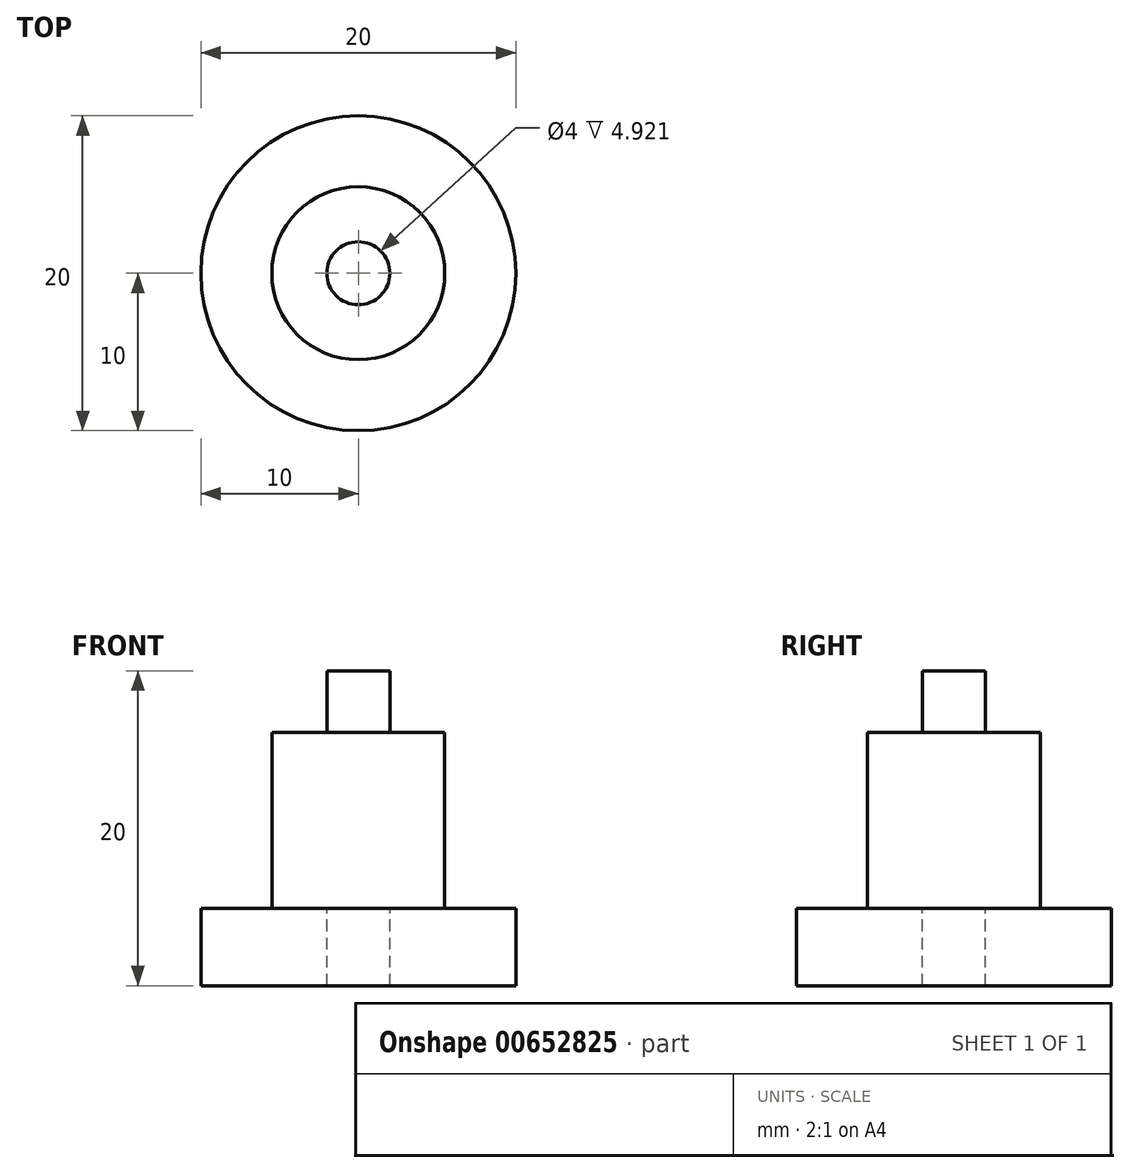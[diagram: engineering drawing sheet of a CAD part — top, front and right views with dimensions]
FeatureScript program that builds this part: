
annotation { "Feature Type Name" : "Feature", "Feature Type Description" : "" }
export const myFeature = defineFeature(function(context is Context, id is Id, definition is map)
    precondition{}
    {
        {
            var Q0;
            Q0=qCreatedBy(makeId("Front.planeOp"),FACE);
            var sketch = newSketch(context, id + "F0", { "sketchPlane" : qUnion([Q0])});
            skLineSegment(sketch, "E0.bottom", {"start": v(0, 2.34) * mm, "end": v(10, 2.34) * mm});
            skLineSegment(sketch, "E0.top", {"start": v(0, -2.26) * mm, "end": v(10, -2.26) * mm});
            skLineSegment(sketch, "E0.left", {"start": v(0, 2.34) * mm, "end": v(0, -2.26) * mm});
            skLineSegment(sketch, "E0.right", {"start": v(10, 2.34) * mm, "end": v(10, -2.26) * mm});
            skLineSegment(sketch, "E1", {"start": v(2, 2.34) * mm, "end": v(2, -2.26) * mm});
            skSolve(sketch);
        }
        {
            var Q0;
            {var subQ0=sQuery(id+"F0.wireOp",EDGE,"E0.right");Q0=makeQuery(id+"F0.imprint","IMPRINT",FACE,{"disambiguationData":[TD([[makeQuery(id+"F0.imprint","IMPRINT",EDGE,{"derivedFrom":subQ0}),-1.0]])]});}
            var Q1;
            Q1=sQuery(id+"F0.wireOp",EDGE,"E0.left");
            revolve(context, id + "F1", {"entities" : qUnion([Q0]), "axis" : qUnion([Q1]), "revolveType" : RevolveType.FULL});
        }
        {
            var Q0;
            Q0=makeQuery(id+"F1.opRevolve","SWEPT_FACE",FACE,{"disambiguationData":[OSD([sQuery(id+"F0.wireOp",EDGE,"E0.bottom")])]});
            var sketch = newSketch(context, id + "F2", { "sketchPlane" : qUnion([Q0])});
            skCircle(sketch, "E2.0", {"center": v(0, 0) * mm, "radius": 5.5 * mm});
            skSolve(sketch);
        }
        {
            var Q0;
            Q0=makeQuery(id+"F2.imprint","IMPRINT",FACE,{"disambiguationData":[TD([[makeQuery(id+"F2.imprint","IMPRINT",EDGE,{"derivedFrom":sQuery(id+"F2.wireOp",EDGE,"E2.0")}),1.0]])]});
            extrude(context, id + "F3", {"entities" : qUnion([Q0]), "operationType" : NewBodyOperationType.ADD, "depth" : .3 * mm, "offsetDistance" : 25 * mm});
        }
        {
            var Q0;
            Q0=qCreatedBy(makeId("Front.planeOp"),FACE);
            var sketch = newSketch(context, id + "F4", { "sketchPlane" : qUnion([Q0])});
            skLineSegment(sketch, "E3.bottom", {"start": v(0, 2.65) * mm, "end": v(5.5, 2.65) * mm});
            skLineSegment(sketch, "E3.top", {"start": v(0, 13.85) * mm, "end": v(5.5, 13.85) * mm});
            skLineSegment(sketch, "E3.left", {"start": v(0, 2.65) * mm, "end": v(0, 13.85) * mm});
            skLineSegment(sketch, "E3.right", {"start": v(5.5, 2.65) * mm, "end": v(5.5, 13.85) * mm});
            skSolve(sketch);
        }
        {
            var Q0;
            Q0 = qSketchRegion(id + "F4", true);
            var Q1;
            Q1=sQuery(id+"F4.wireOp",EDGE,"E3.left");
            revolve(context, id + "F5", {"entities" : qUnion([Q0]), "axis" : qUnion([Q1]), "revolveType" : RevolveType.FULL});
        }
        {
            var Q0;
            Q0=makeQuery(id+"F5.opRevolve","SWEPT_FACE",FACE,{"disambiguationData":[OSD([sQuery(id+"F4.wireOp",EDGE,"E3.top")])]});
            var sketch = newSketch(context, id + "F6", { "sketchPlane" : qUnion([Q0])});
            skCircle(sketch, "E4.0", {"center": v(0, 0) * mm, "radius": 2 * mm});
            skSolve(sketch);
        }
        {
            var Q0;
            Q0=makeQuery(id+"F6.imprint","IMPRINT",FACE,{"disambiguationData":[TD([[makeQuery(id+"F6.imprint","IMPRINT",EDGE,{"derivedFrom":sQuery(id+"F6.wireOp",EDGE,"E4.0")}),1.0]])]});
            extrude(context, id + "F7", {"entities" : qUnion([Q0]), "operationType" : NewBodyOperationType.ADD, "depth" : 3.9 * mm, "offsetDistance" : 25 * mm});
        }
        {
            var Q0;
            Q0=qCreatedBy(makeId("Front.planeOp"),FACE);
            var sketch = newSketch(context, id + "F8", { "sketchPlane" : qUnion([Q0])});
            skLineSegment(sketch, "E5", {"start": v(0, 17.77) * mm, "end": v(2, 17.77) * mm});
            skLineSegment(sketch, "E6", {"start": v(2, 17.77) * mm, "end": v(2, 13.87) * mm});
            skLineSegment(sketch, "E7", {"start": v(2, 13.87) * mm, "end": v(5.5, 13.87) * mm});
            skLineSegment(sketch, "E8", {"start": v(5.5, 13.87) * mm, "end": v(5.5, 2.67) * mm});
            skLineSegment(sketch, "E9", {"start": v(5.5, 2.67) * mm, "end": v(10, 2.67) * mm});
            skLineSegment(sketch, "E10", {"start": v(10, 2.67) * mm, "end": v(10, -2.23) * mm});
            skLineSegment(sketch, "E11", {"start": v(10, -2.23) * mm, "end": v(2, -2.23) * mm});
            skLineSegment(sketch, "E12", {"start": v(2, -2.23) * mm, "end": v(2, 2.7) * mm});
            skLineSegment(sketch, "E13", {"start": v(2, 2.7) * mm, "end": v(0, 2.7) * mm});
            skLineSegment(sketch, "E14", {"start": v(0, 2.7) * mm, "end": v(0, 17.77) * mm});
            skLineSegment(sketch, "E15", {"start": v(0, 23.76) * mm, "end": v(0, -14.34) * mm});
            skSolve(sketch);
        }
        {
            var Q0;
            {var subQ0=sQuery(id+"F8.wireOp",EDGE,"E5");Q0=makeQuery(id+"F8.imprint","IMPRINT",FACE,{"disambiguationData":[TD([[makeQuery(id+"F8.imprint","IMPRINT",EDGE,{"derivedFrom":subQ0}),-1.0]])]});}
            var Q1;
            Q1=sQuery(id+"F8.wireOp",EDGE,"E15");
            revolve(context, id + "F9", {"entities" : qUnion([Q0]), "axis" : qUnion([Q1]), "revolveType" : RevolveType.FULL});
        }
        {
            var Q0;
            Q0=makeQuery(id+"F1.opRevolve","SWEPT_BODY",BODY,{"disambiguationData":[OSD([sQuery(id+"F0.wireOp",EDGE,"E0.bottom"),sQuery(id+"F0.wireOp",EDGE,"E0.top"),sQuery(id+"F0.wireOp",EDGE,"E0.right"),sQuery(id+"F0.wireOp",EDGE,"E1")])]});
            var Q1;
            Q1=makeQuery(id+"F5.opRevolve","SWEPT_BODY",BODY,{"disambiguationData":[OSD([sQuery(id+"F4.wireOp",EDGE,"E3.bottom"),sQuery(id+"F4.wireOp",EDGE,"E3.top"),sQuery(id+"F4.wireOp",EDGE,"E3.left"),sQuery(id+"F4.wireOp",EDGE,"E3.right")])]});
            deleteBodies(context, id + "F10", {"entities" : qUnion([Q0, Q1])});
        }
    });
